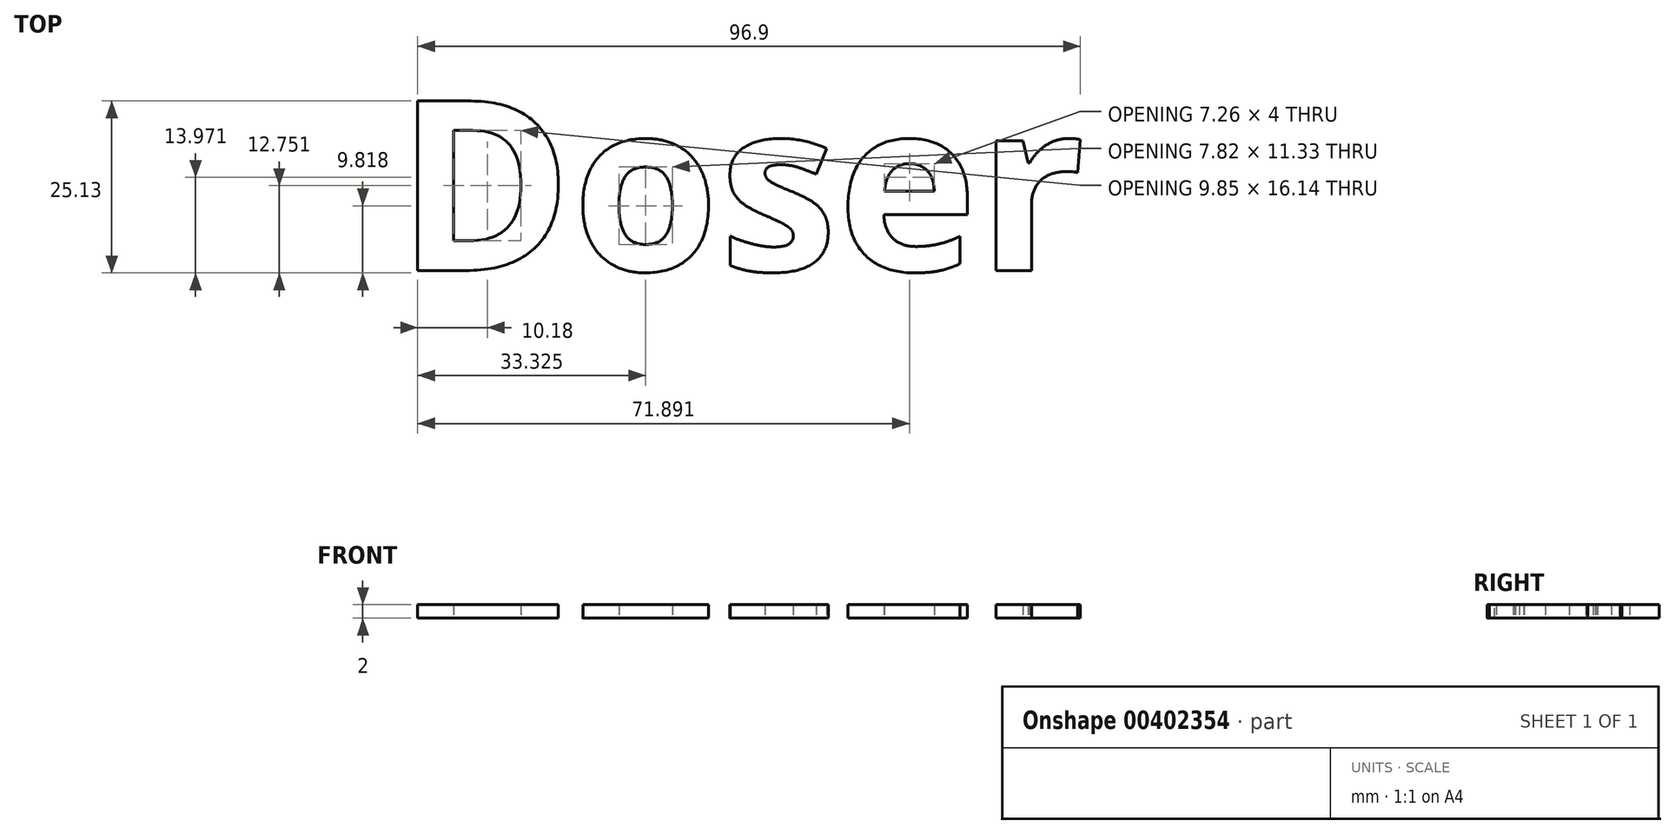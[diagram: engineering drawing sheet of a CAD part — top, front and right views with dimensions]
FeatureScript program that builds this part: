
annotation { "Feature Type Name" : "Feature", "Feature Type Description" : "" }
export const myFeature = defineFeature(function(context is Context, id is Id, definition is map)
    precondition{}
    {
        {
            var Q0;
            Q0=qCreatedBy(makeId("Top.planeOp"),FACE);
            var sketch = newSketch(context, id + "F0", { "sketchPlane" : qUnion([Q0])});
            skText(sketch, "E0", { "text": "Doser", "fontName": "OpenSans-Bold.ttf"});
            const initialGuessF0  = {"E0": [-0.05113, -0.0125, 1, 0, 0.025]};
            skSetInitialGuess(sketch, initialGuessF0);
            skSolve(sketch);
        }
        {
            var Q0;
            Q0 = qSketchRegion(id + "F0", true);
            extrude(context, id + "F1", {"entities" : qUnion([Q0]), "depth" : 2 * mm});
        }
    });
